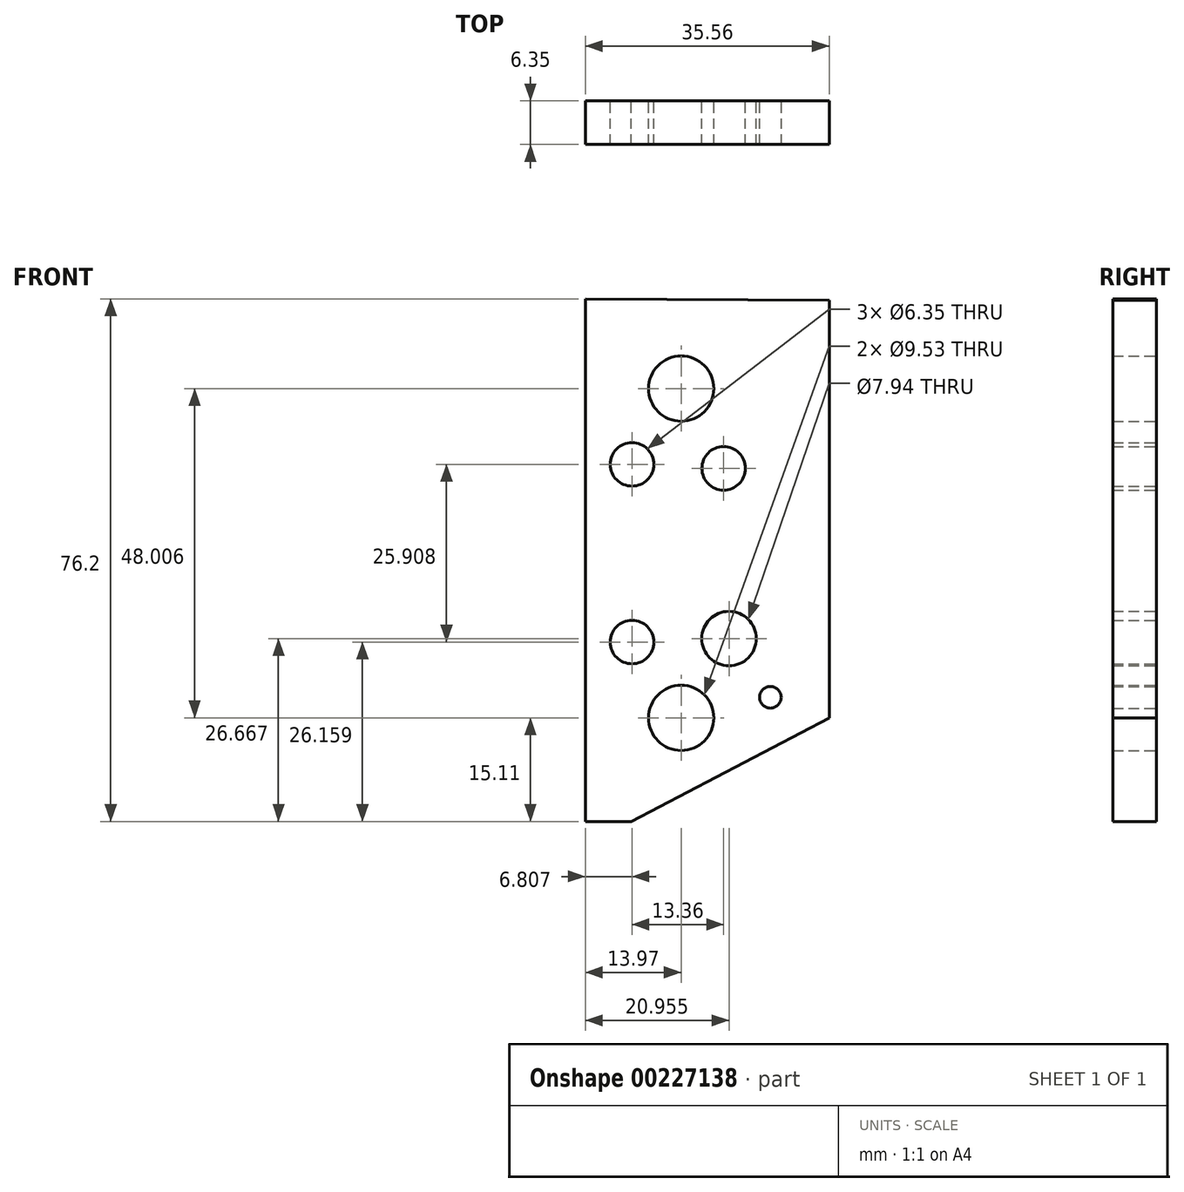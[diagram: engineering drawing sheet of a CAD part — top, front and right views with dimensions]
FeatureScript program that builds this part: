
annotation { "Feature Type Name" : "Feature", "Feature Type Description" : "" }
export const myFeature = defineFeature(function(context is Context, id is Id, definition is map)
    precondition{}
    {
        {
            var Q0;
            Q0=qCreatedBy(makeId("Front.planeOp"),FACE);
            var sketch = newSketch(context, id + "F0", { "sketchPlane" : qUnion([Q0])});
            skCircle(sketch, "E0", {"center": v(0, 0) * mm, "radius": 4.76 * mm});
            skCircle(sketch, "E1", {"center": v(0, 48) * mm, "radius": 4.76 * mm});
            skLineSegment(sketch, "E2", {"start": v(-13.97, -15.1) * mm, "end": v(-13.97, 61.1) * mm});
            skLineSegment(sketch, "E3", {"start": v(21.59, 0) * mm, "end": v(21.59, 60.86) * mm});
            skLineSegment(sketch, "E4", {"start": v(21.59, 60.86) * mm, "end": v(-13.97, 61.1) * mm});
            skLineSegment(sketch, "E5", {"start": v(-13.97, -15.1) * mm, "end": v(-7.29, -15.1) * mm});
            skLineSegment(sketch, "E6", {"start": v(-7.29, -15.1) * mm, "end": v(21.6, 0) * mm});
            skCircle(sketch, "E7", {"center": v(13, 3) * mm, "radius": 1.59 * mm});
            skCircle(sketch, "E8", {"center": v(6.99, 11.56) * mm, "radius": 3.97 * mm});
            skCircle(sketch, "E9", {"center": v(-7.16, 11.05) * mm, "radius": 3.18 * mm});
            skCircle(sketch, "E10", {"center": v(6.2, 36.37) * mm, "radius": 3.18 * mm});
            skCircle(sketch, "E11", {"center": v(-7.16, 36.96) * mm, "radius": 3.18 * mm});
            skSolve(sketch);
        }
        {
            var Q0;
            Q0=makeQuery(id+"F0.imprint","IMPRINT",FACE,{"disambiguationData":[TD([[makeQuery(id+"F0.imprint","IMPRINT",EDGE,{"derivedFrom":sQuery(id+"F0.wireOp",EDGE,"E0")}),-1.0]])]});
            extrude(context, id + "F1", {"entities" : qUnion([Q0]), "depth" : 6.35 * mm});
        }
    });
